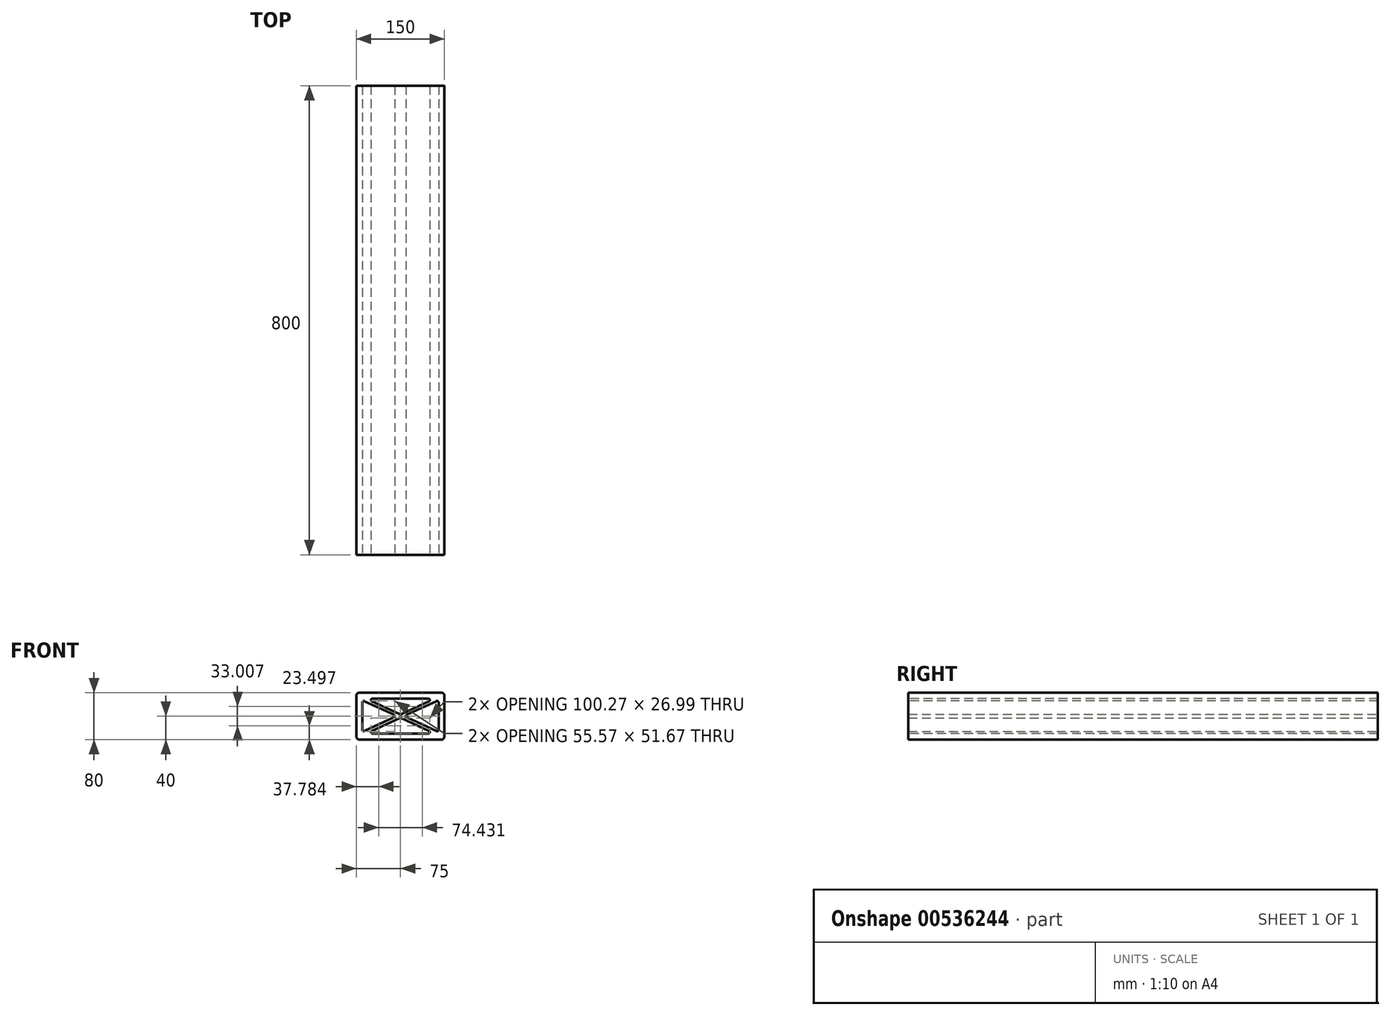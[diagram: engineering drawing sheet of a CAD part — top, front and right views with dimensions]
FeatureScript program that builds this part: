
annotation { "Feature Type Name" : "Feature", "Feature Type Description" : "" }
export const myFeature = defineFeature(function(context is Context, id is Id, definition is map)
    precondition{}
    {
        {
            var Q0;
            Q0=qCreatedBy(makeId("Front.planeOp"),FACE);
            var sketch = newSketch(context, id + "F0", { "sketchPlane" : qUnion([Q0])});
            skLineSegment(sketch, "E0.bottom", {"start": v(-75, 40) * mm, "end": v(75, 40) * mm});
            skLineSegment(sketch, "E0.top", {"start": v(-75, -40) * mm, "end": v(75, -40) * mm});
            skLineSegment(sketch, "E0.left", {"start": v(-75, 40) * mm, "end": v(-75, -40) * mm});
            skLineSegment(sketch, "E0.right", {"start": v(75, 40) * mm, "end": v(75, -40) * mm});
            skPoint(sketch, "E0.middle", {"position": v(0, 0) * mm});
            skSolve(sketch);
        }
        {
            var Q0;
            Q0 = qSketchRegion(id + "F0", true);
            extrude(context, id + "F1", {"entities" : qUnion([Q0]), "depth" : 800 * mm, "offsetDistance" : 25 * mm});
        }
        {
            var Q0;
            Q0=makeQuery(id+"F1.opExtrude","CAP_FACE",FACE,{"disambiguationData":[OSD([sQuery(id+"F0.wireOp",EDGE,"E0.bottom"),sQuery(id+"F0.wireOp",EDGE,"E0.top"),sQuery(id+"F0.wireOp",EDGE,"E0.left"),sQuery(id+"F0.wireOp",EDGE,"E0.right")])],"isStart":false});
            var sketch = newSketch(context, id + "F2", { "sketchPlane" : qUnion([Q0])});
            skLineSegment(sketch, "E1.bottom", {"start": v(-59.03, 30) * mm, "end": v(59.03, 30) * mm});
            skLineSegment(sketch, "E1.top", {"start": v(-59.03, -30) * mm, "end": v(59.03, -30) * mm});
            skLineSegment(sketch, "E1.left", {"start": v(-65, 27.25) * mm, "end": v(-65, -27.25) * mm});
            skLineSegment(sketch, "E1.right", {"start": v(65, 27.25) * mm, "end": v(65, -27.25) * mm});
            skLineSegment(sketch, "E2", {"start": v(-65, -30) * mm, "end": v(65, 30) * mm, "construction": true});
            skLineSegment(sketch, "E3", {"start": v(-65, 30) * mm, "end": v(65, -30) * mm, "construction": true});
            skLineSegment(sketch, "E4.0", {"start": v(-59.03, -30) * mm, "end": v(0, -2.75) * mm});
            skLineSegment(sketch, "E5.0", {"start": v(-65, -27.25) * mm, "end": v(-5.97, 0) * mm});
            skLineSegment(sketch, "E6.0", {"start": v(-65, 27.25) * mm, "end": v(-5.97, 0) * mm});
            skLineSegment(sketch, "E7.0", {"start": v(-59.03, 30) * mm, "end": v(0, 2.75) * mm});
            skLineSegment(sketch, "E8.trimOffspring", {"start": v(0, 2.75) * mm, "end": v(59.03, 30) * mm});
            skLineSegment(sketch, "E9.trimOffspring", {"start": v(5.97, 0) * mm, "end": v(65, 27.25) * mm});
            skLineSegment(sketch, "E10.trimOffspring", {"start": v(5.97, 0) * mm, "end": v(65, -27.25) * mm});
            skLineSegment(sketch, "E11.trimOffspring", {"start": v(0, -2.75) * mm, "end": v(59.03, -30) * mm});
            skSolve(sketch);
        }
        {
            var Q0;
            Q0 = qSketchRegion(id + "F2", true);
            extrude(context, id + "F3", {"entities" : qUnion([Q0]), "operationType" : NewBodyOperationType.REMOVE, "endBound" : BoundingType.THROUGH_ALL, "oppositeDirection" : true, "depth" : 25 * mm, "offsetDistance" : 25 * mm});
        }
        {
            var Q0;
            Q0=makeQuery(id+"F3.boolean.opBoolean","COPY",EDGE,{"derivedFrom":makeQuery(id+"F3.opExtrude","SWEPT_EDGE",EDGE,{"disambiguationData":[OSD([sQuery(id+"F2.wireOp",EDGE,"E1.bottom"),sQuery(id+"F2.wireOp",EDGE,"E7.0")])]})});
            var Q1;
            Q1=makeQuery(id+"F3.boolean.opBoolean","COPY",EDGE,{"derivedFrom":makeQuery(id+"F3.opExtrude","SWEPT_EDGE",EDGE,{"disambiguationData":[OSD([sQuery(id+"F2.wireOp",EDGE,"E9.trimOffspring"),sQuery(id+"F2.wireOp",EDGE,"E10.trimOffspring")])]})});
            var Q2;
            Q2=makeQuery(id+"F3.boolean.opBoolean","COPY",EDGE,{"derivedFrom":makeQuery(id+"F3.opExtrude","SWEPT_EDGE",EDGE,{"disambiguationData":[OSD([sQuery(id+"F2.wireOp",EDGE,"E4.0"),sQuery(id+"F2.wireOp",EDGE,"E11.trimOffspring")])]})});
            var Q3;
            Q3=makeQuery(id+"F3.boolean.opBoolean","COPY",EDGE,{"derivedFrom":makeQuery(id+"F3.opExtrude","SWEPT_EDGE",EDGE,{"disambiguationData":[OSD([sQuery(id+"F2.wireOp",EDGE,"E5.0"),sQuery(id+"F2.wireOp",EDGE,"E6.0")])]})});
            var Q4;
            Q4=makeQuery(id+"F3.boolean.opBoolean","COPY",EDGE,{"derivedFrom":makeQuery(id+"F3.opExtrude","SWEPT_EDGE",EDGE,{"disambiguationData":[OSD([sQuery(id+"F2.wireOp",EDGE,"E7.0"),sQuery(id+"F2.wireOp",EDGE,"E8.trimOffspring")])]})});
            var Q5;
            Q5=makeQuery(id+"F3.boolean.opBoolean","COPY",EDGE,{"derivedFrom":makeQuery(id+"F3.opExtrude","SWEPT_EDGE",EDGE,{"disambiguationData":[OSD([sQuery(id+"F2.wireOp",EDGE,"E1.right"),sQuery(id+"F2.wireOp",EDGE,"E10.trimOffspring")])]})});
            var Q6;
            Q6=makeQuery(id+"F3.boolean.opBoolean","COPY",EDGE,{"derivedFrom":makeQuery(id+"F3.opExtrude","SWEPT_EDGE",EDGE,{"disambiguationData":[OSD([sQuery(id+"F2.wireOp",EDGE,"E1.right"),sQuery(id+"F2.wireOp",EDGE,"E9.trimOffspring")])]})});
            var Q7;
            Q7=makeQuery(id+"F3.boolean.opBoolean","COPY",EDGE,{"derivedFrom":makeQuery(id+"F3.opExtrude","SWEPT_EDGE",EDGE,{"disambiguationData":[OSD([sQuery(id+"F2.wireOp",EDGE,"E1.bottom"),sQuery(id+"F2.wireOp",EDGE,"E8.trimOffspring")])]})});
            var Q8;
            Q8=makeQuery(id+"F3.boolean.opBoolean","COPY",EDGE,{"derivedFrom":makeQuery(id+"F3.opExtrude","SWEPT_EDGE",EDGE,{"disambiguationData":[OSD([sQuery(id+"F2.wireOp",EDGE,"E1.left"),sQuery(id+"F2.wireOp",EDGE,"E6.0")])]})});
            var Q9;
            Q9=makeQuery(id+"F3.boolean.opBoolean","COPY",EDGE,{"derivedFrom":makeQuery(id+"F3.opExtrude","SWEPT_EDGE",EDGE,{"disambiguationData":[OSD([sQuery(id+"F2.wireOp",EDGE,"E1.left"),sQuery(id+"F2.wireOp",EDGE,"E5.0")])]})});
            var Q10;
            Q10=makeQuery(id+"F3.boolean.opBoolean","COPY",EDGE,{"derivedFrom":makeQuery(id+"F3.opExtrude","SWEPT_EDGE",EDGE,{"disambiguationData":[OSD([sQuery(id+"F2.wireOp",EDGE,"E1.top"),sQuery(id+"F2.wireOp",EDGE,"E4.0")])]})});
            var Q11;
            Q11=makeQuery(id+"F3.boolean.opBoolean","COPY",EDGE,{"derivedFrom":makeQuery(id+"F3.opExtrude","SWEPT_EDGE",EDGE,{"disambiguationData":[OSD([sQuery(id+"F2.wireOp",EDGE,"E1.top"),sQuery(id+"F2.wireOp",EDGE,"E11.trimOffspring")])]})});
            fillet(context, id + "F4", {"entities" : qUnion([Q0, Q1, Q2, Q3, Q4, Q5, Q6, Q7, Q8, Q9, Q10, Q11]), "radius" : 2.5 * mm, "tangentPropagation" : true, "allowEdgeOverflow" : false});
        }
        {
            var Q0;
            Q0=makeQuery(id+"F1.opExtrude","SWEPT_EDGE",EDGE,{"disambiguationData":[OSD([sQuery(id+"F0.wireOp",EDGE,"E0.bottom"),sQuery(id+"F0.wireOp",EDGE,"E0.left")])]});
            var Q1;
            Q1=makeQuery(id+"F1.opExtrude","SWEPT_EDGE",EDGE,{"disambiguationData":[OSD([sQuery(id+"F0.wireOp",EDGE,"E0.top"),sQuery(id+"F0.wireOp",EDGE,"E0.left")])]});
            var Q2;
            Q2=makeQuery(id+"F1.opExtrude","SWEPT_EDGE",EDGE,{"disambiguationData":[OSD([sQuery(id+"F0.wireOp",EDGE,"E0.bottom"),sQuery(id+"F0.wireOp",EDGE,"E0.right")])]});
            var Q3;
            Q3=makeQuery(id+"F1.opExtrude","SWEPT_EDGE",EDGE,{"disambiguationData":[OSD([sQuery(id+"F0.wireOp",EDGE,"E0.top"),sQuery(id+"F0.wireOp",EDGE,"E0.right")])]});
            fillet(context, id + "F5", {"entities" : qUnion([Q0, Q1, Q2, Q3]), "radius" : 5 * mm, "tangentPropagation" : true, "allowEdgeOverflow" : false});
        }
    });
